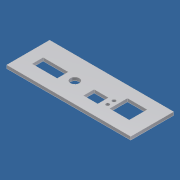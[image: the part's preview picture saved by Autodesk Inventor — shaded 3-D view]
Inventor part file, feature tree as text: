
AUTODESK INVENTOR PART (.ipt)
format: ipt  version: unknown  size: 203,776 bytes
history: native  units: mm
features: extrude x2, sketch x2
ambient origin geometry x8: Origin, YZ Plane, XZ Plane, XY Plane, X Axis, Y Axis, Z Axis, Center Point
bodies: Volumenkörper1 (feature_tree)
feature tree (4):
  extrude  "Extrusion1"  Depth=68.8mm
  extrude  "Extrusion2"  Depth=6.5mm
  sketch  "Skizze1"  dims[d0=23.8mm d1=68.8mm]
  sketch  "Skizze2"  dims[d2=1.8mm d3=0.0mm d5=6.5mm d6=20.5mm d7=7.5mm d8=13.7mm d9=11.3mm d10=5.0mm d11=26.5mm d12=47.0mm d13=47.0mm d14=2.0mm d15=2.0mm d16=3.5mm d17=9.0mm d18=49.5mm d19=60.5mm d20=7.5mm d21=17.5mm d22=6.5mm d23=12.5mm d24=36.0mm d25=44.0mm d26=1.8mm d27=0.0mm]
